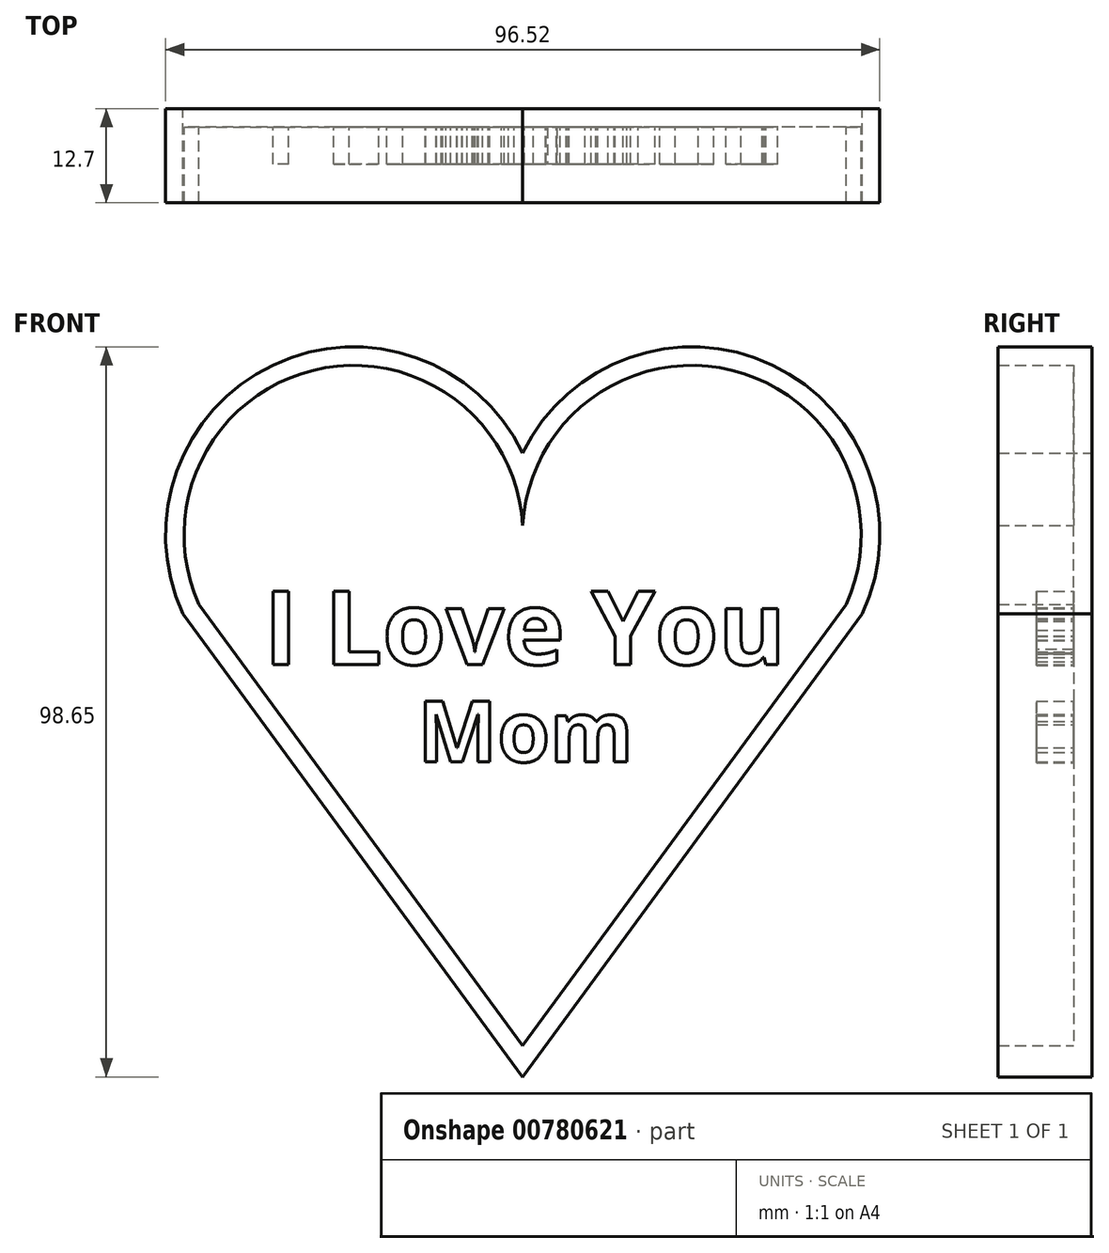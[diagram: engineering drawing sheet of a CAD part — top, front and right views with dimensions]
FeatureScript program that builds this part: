
annotation { "Feature Type Name" : "Feature", "Feature Type Description" : "" }
export const myFeature = defineFeature(function(context is Context, id is Id, definition is map)
    precondition{}
    {
        {
            var Q0;
            Q0=qCreatedBy(makeId("Front.planeOp"),FACE);
            var sketch = newSketch(context, id + "F0", { "sketchPlane" : qUnion([Q0])});
            skArc(sketch, "E0", {"start": v(45.9, 6.83) * mm, "mid": v(33.74, 40.47) * mm, "end": v(0, 28.57) * mm});
            skArc(sketch, "E1.MirrorC", {"start": v(-45.9, 6.83) * mm, "mid": v(-33.74, 40.47) * mm, "end": v(0, 28.57) * mm});
            skLineSegment(sketch, "E2", {"start": v(-45.9, 6.83) * mm, "end": v(0, -55.74) * mm});
            skLineSegment(sketch, "E3", {"start": v(45.9, 6.83) * mm, "end": v(0, -55.74) * mm});
            skSolve(sketch);
        }
        {
            var Q0;
            Q0=makeQuery(id+"F0.imprint","IMPRINT",FACE,{"disambiguationData":[TD([[makeQuery(id+"F0.imprint","IMPRINT",EDGE,{"derivedFrom":sQuery(id+"F0.wireOp",EDGE,"E0")}),1.0]])]});
            extrude(context, id + "F1", {"entities" : qUnion([Q0]), "depth" : 12.7 * mm, "offsetDistance" : 25.4 * mm});
        }
        {
            var Q0;
            Q0=makeQuery(id+"F1.opExtrude","CAP_FACE",FACE,{"disambiguationData":[OSD([sQuery(id+"F0.wireOp",EDGE,"E0"),sQuery(id+"F0.wireOp",EDGE,"E1.MirrorC"),sQuery(id+"F0.wireOp",EDGE,"E2"),sQuery(id+"F0.wireOp",EDGE,"E3")])],"isStart":false});
            shell(context, id + "F2", {"entities" : qUnion([Q0]), "thickness" : 2.5 * mm});
        }
        {
            var Q0;
            Q0=makeQuery(id+"F2.opShell","OFFSET_FACE",FACE,{"disambiguationData":[OSD([sQuery(id+"F0.wireOp",EDGE,"E0"),sQuery(id+"F0.wireOp",EDGE,"E1.MirrorC"),sQuery(id+"F0.wireOp",EDGE,"E2"),sQuery(id+"F0.wireOp",EDGE,"E3")])]});
            var sketch = newSketch(context, id + "F3", { "sketchPlane" : qUnion([Q0])});
            skText(sketch, "E4", { "text": "I Love You", "fontName": "OpenSans-Bold.ttf"});
            skText(sketch, "E5", { "text": "Mom", "fontName": "OpenSans-Bold.ttf"});
            const initialGuessF3  = {"E4": [-0.03495, 0, 1, 0, 0.00996], "E5": [-0.0142, -0.01316, 1, 0, 0.00824]};
            skSetInitialGuess(sketch, initialGuessF3);
            skSolve(sketch);
        }
        {
            var Q0;
            Q0 = qSketchRegion(id + "F3", true);
            extrude(context, id + "F4", {"entities" : qUnion([Q0]), "operationType" : NewBodyOperationType.ADD, "depth" : 5 * mm, "offsetDistance" : 25 * mm});
        }
    });
